# Revit family: Hager-UNIVERS-Surface_mounted-IP44-With_Cover-With_DIN-Hosted-AT-de
name_source: partatom
category: Electrical Equipment
units: mm (PartAtom-declared; Revit-internal decimal feet)

## family parameters
Cut with Voids When Loaded = No
Host = Face
Maintain Annotation Orientation = Yes
Panel Configuration = Two Columns, Circuits Across
Part Type = Panelboard
Room Calculation Point = No
Round Connector Dimension = Use Diameter
Shared = No

## types (7) — shared parameters
BC_MODEL_ID = 1554447
BC_OBJECT_ID = 513925
BC_OBJECT_VERSION = #3
Code hager = ADD-EC000214_EU
EF000003 - Montageart = Aufputz
EF000008 - Breite = 550 mm  [stored 1.80446 ft]
EF000024 - UV-beständig = No
EF000049 - Tiefe = 161 mm  [stored 0.528215 ft]
EF000116 - RAL-Nummer = 9010
EF000118 - Mit Montageplatte = No
EF001062 - EMV-Ausführung = No
EF001088 - Anbaumöglichkeit = Yes
EF001134 - DIN-Schiene = Yes
EF002950 - Breite in Teilungseinheiten = 24
EF005474 - Schutzart (IP) = IP44
EF006244 - Transparenter Deckel/Tür = No
EF006306 - Mit Schloss = No
EF015776 - Erdungsklemmenblock = No
EF015777 - Neutralleiterklemmenblock = No
EF015941 - Signaldurchlassende Tür = No
ETIM class code = EC000214
ETIM class name = Small distribution board
HG000001-Anzahl der Spalten = 1
HG000002-Mit tür = Yes
HG000003-Bereich = UNIVERS
HG000005-Dicke = 2 mm  [stored 0.00656168 ft]
HG000006-Unterputz = No
HG000009-Doppelflügeligen Tür = No
HG000010-Asymmetrische Türen = No
HG000011-Leere Reihen von unten = No
HG000012-Türschwenkwinkel = 90.00°
HG000013-Tür links = No
HG000014-Tür rechts = Yes
HG000015-Sichtbarkeit der Türöffnung = Yes
HG000016-3D-Türsichtbarkeit = Yes
HG000017-Distanz zwischen den Polen = 18 mm  [stored 0.0590551 ft]
HG000060-RAL-number = 9010
HG000099-Onfly Template ID-de-AT = 507532
HGEF0002950-Breite in Teilungseinheiten = 24
Manufacturer = Hager
Name = UNIVERS-Surface_mounted-IP44-With_Cover-With_DIN-AT
Name BIM&CO = Electricity
Name hager = ADD_Enclosures_EC000214
Uniformat = Low Tension Service & Dist.
Uniformat code = D501001
zero-valued in all types: Default Elevation, EF000218 - Einbautiefe, EF000332 - Einbauhöhe, EF000846 - Einbaubreite, EF001131 - Innentiefe, HG000007-Anzahl der leeren Spalten

## per-type parameters (varying)
| type | BC_VARIANT_ID | EF000007 - Farbe | EF000040 - Höhe | EF000266 - Anzahl der Reihen | HG000004-Herstellerreferenz | HG000008-Anzahl der leeren Reihen | HGEF000266-Anzahl der Reihen |
| UNIVERS-Surface_mounted_W550_H650_D161_24_Modular_Spacing-FWQ42M2 | 1179162 | weiß | 650 mm  [stored 2.13255 ft] | 4 | FWQ42M2 | 0 | 4 |
| UNIVERS-Surface_mounted_W550_H800_D161_24_Modular_Spacing-FWQ52M2 | 1179163 | weiß | 800 mm  [stored 2.62467 ft] | 5 | FWQ52M2 | 0 | 5 |
| UNIVERS-Surface_mounted_W550_H800_D161_24_Modular_Spacing-FWQ52N2 | 1179165 |  | 800 mm  [stored 2.62467 ft] | 5 | FWQ52N2 | 2 | 5 |
| UNIVERS-Surface_mounted_W550_H950_D161_24_Modular_Spacing-FWQ62M2 | 1179166 | weiß | 950 mm  [stored 3.1168 ft] | 6 | FWQ62M2 | 0 | 6 |
| UNIVERS-Surface_mounted_W550_H950_D161_24_Modular_Spacing-FWQ62N2 | 1179167 |  | 950 mm  [stored 3.1168 ft] | 6 | FWQ62N2 | 2 | 6 |
| UNIVERS-Surface_mounted_W550_H1100_D161_24_Modular_Spacing-FWQ72M2 | 1179170 | weiß | 1100 mm  [stored 3.60892 ft] | 7 | FWQ72M2 | 0 | 7 |
| UNIVERS-Surface_mounted_W550_H1100_D161_24_Modular_Spacing-FWQ72N2 | 1179171 |  | 1100 mm  [stored 3.60892 ft] | 7 | FWQ72N2 | 2 | 7 |

note: column(s) folded — value = type name in every type: Reference

note: [stored X ft] marks values corroborated as IEEE doubles in the binary element streams (Revit-internal decimal feet)

## geometry (parser evidence)
native form markers: Sweep x15
no freeform markers — native parametric forms only
